# Revit family: 208_UVLA  _
name_source: partatom
category: Air Terminals
units: mm (PartAtom-declared; Revit-internal decimal feet)

## family parameters
Always vertical = Yes
Cut with Voids When Loaded = No
Part Type = Normal
Room Calculation Point = Yes
Round Connector Dimension = Use Diameter
Shared = No
Work Plane-Based = No

## types (5) — shared parameters
CAT0 = Yes
CL_Location_5000 = 5000 mm  [stored 16.4042 ft]
Description = CHROME NICKEL-PLATED AIR INTAKE WALL MOUNTED WITH OVERLAP
L1 = 10 mm  [stored 0.0328084 ft]
L_ARR = 400 mm  [stored 1.31234 ft]
Manufacturer = Alnor
QmdConnectorList = 201;D
URL = http://www.ventilation-alnor.co.uk
W_ARR = 400 mm  [stored 1.31234 ft]
XRefLineVPlnId = 7453
YRefLineVPlnId = 7456
magiPartTypeId = 208
magiProductFamilyId = UVLA  *
zero-valued in all types: CLBTZ, H_ARR

## per-type parameters (varying)
| type | BGD | D | R2 |
| UVLA  100 | 67 mm | 100 mm | 60 mm |
| UVLA  200 | 127 mm | 200 mm | 110 mm |
| UVLA  160 | 96 mm | 160 mm | 88 mm |
| UVLA  150 | 96 mm | 150 mm | 90 mm |
| UVLA  125 | 83 mm | 125 mm | 75 mm |

note: column(s) folded — value = type name in every type: MC Product Code, magiProductId

note: [stored X ft] marks values corroborated as IEEE doubles in the binary element streams (Revit-internal decimal feet)

## geometry (parser evidence)
native form markers: Blend x4, Sweep x2
no freeform markers — native parametric forms only
